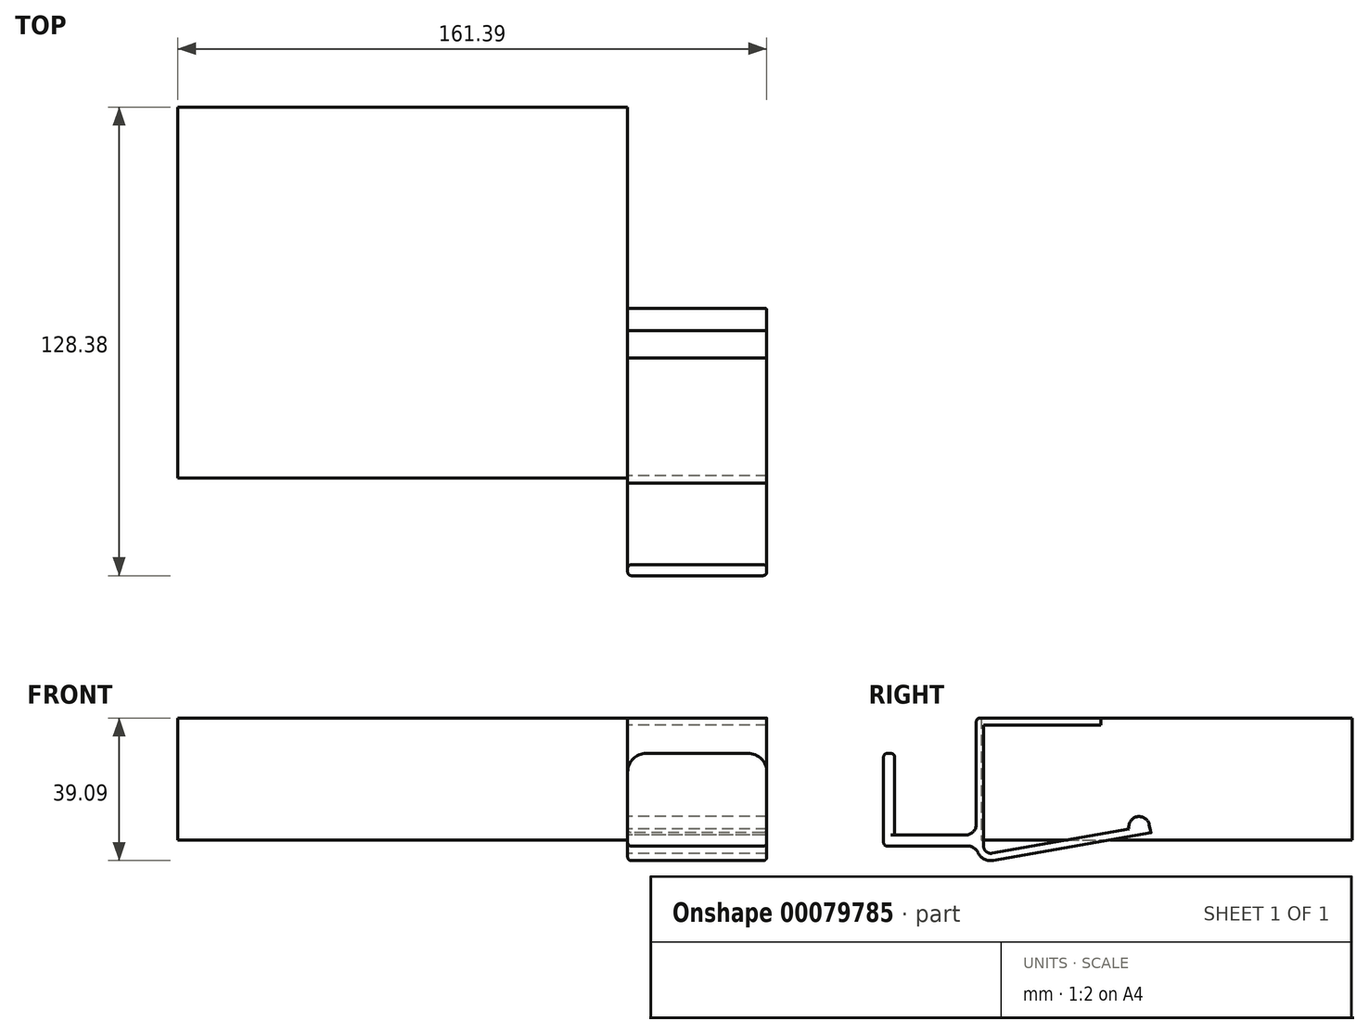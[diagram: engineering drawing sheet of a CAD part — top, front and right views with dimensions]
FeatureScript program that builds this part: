
annotation { "Feature Type Name" : "Feature", "Feature Type Description" : "" }
export const myFeature = defineFeature(function(context is Context, id is Id, definition is map)
    precondition{}
    {
        {
            var Q0;
            Q0=qCreatedBy(makeId("Right.planeOp"),FACE);
            var sketch = newSketch(context, id + "F0", { "sketchPlane" : qUnion([Q0])});
            skLineSegment(sketch, "E0.bottom", {"start": v(-53.16, 8.17) * mm, "end": v(48.44, 8.17) * mm});
            skLineSegment(sketch, "E0.top", {"start": v(-53.16, -25.23) * mm, "end": v(48.44, -25.23) * mm});
            skLineSegment(sketch, "E0.left", {"start": v(-53.16, 8.17) * mm, "end": v(-53.16, -25.23) * mm});
            skLineSegment(sketch, "E0.right", {"start": v(48.44, 8.17) * mm, "end": v(48.44, -25.23) * mm});
            skSolve(sketch);
        }
        {
            var Q0;
            Q0=makeQuery(id+"F0.imprint","IMPRINT",FACE,{"disambiguationData":[TD([[makeQuery(id+"F0.imprint","IMPRINT",EDGE,{"derivedFrom":sQuery(id+"F0.wireOp",EDGE,"E0.bottom")}),-1.0]])]});
            extrude(context, id + "F1", {"entities" : qUnion([Q0]), "depth" : 123.3 * mm});
        }
        {
            var Q0;
            Q0=makeQuery(id+"F1.opExtrude","CAP_FACE",FACE,{"disambiguationData":[OSD([sQuery(id+"F0.wireOp",EDGE,"E0.bottom"),sQuery(id+"F0.wireOp",EDGE,"E0.top"),sQuery(id+"F0.wireOp",EDGE,"E0.left"),sQuery(id+"F0.wireOp",EDGE,"E0.right")])],"isStart":false});
            var sketch = newSketch(context, id + "F2", { "sketchPlane" : qUnion([Q0])});
            skLineSegment(sketch, "E1", {"start": v(-20.37, 8.17) * mm, "end": v(-53.54, 8.17) * mm});
            skLineSegment(sketch, "E2", {"start": v(-54.54, 7.17) * mm, "end": v(-54.54, -23.92) * mm});
            skLineSegment(sketch, "E3", {"start": v(-49.85, -30.86) * mm, "end": v(-6.7, -23.25) * mm});
            skLineSegment(sketch, "E4.0", {"start": v(-20.37, 6.17) * mm, "end": v(-52.54, 6.17) * mm});
            skLineSegment(sketch, "E5.0", {"start": v(-52.54, 6.17) * mm, "end": v(-52.54, -26.92) * mm});
            skArc(sketch, "E6", {"start": v(-7.2, -21.03) * mm, "mid": v(-10.57, -18.9) * mm, "end": v(-12.7, -22.28) * mm});
            skLineSegment(sketch, "E7", {"start": v(-7.2, -21.03) * mm, "end": v(-6.7, -23.25) * mm});
            skLineSegment(sketch, "E8", {"start": v(-20.37, 8.17) * mm, "end": v(-20.37, 6.17) * mm});
            skLineSegment(sketch, "E9.trimOffspring", {"start": v(-50.2, -28.9) * mm, "end": v(-12.7, -22.28) * mm});
            skPoint(sketch, "E10.visualSharp", {"position": v(-54.54, -31.7) * mm});
            skArc(sketch, "E10.filletArc", {"start": v(-54.54, -26.92) * mm, "mid": v(-53.11, -29.99) * mm, "end": v(-49.85, -30.86) * mm});
            skPoint(sketch, "E11.visualSharp", {"position": v(-52.54, -29.3) * mm});
            skArc(sketch, "E11.filletArc", {"start": v(-52.54, -26.92) * mm, "mid": v(-51.83, -28.46) * mm, "end": v(-50.2, -28.9) * mm});
            skPoint(sketch, "E12.visualSharp", {"position": v(-54.54, 8.17) * mm});
            skArc(sketch, "E12.filletArc", {"start": v(-53.54, 8.17) * mm, "mid": v(-54.25, 7.88) * mm, "end": v(-54.54, 7.17) * mm});
            skLineSegment(sketch, "E13", {"start": v(-54.54, -26.92) * mm, "end": v(-79.94, -26.92) * mm});
            skLineSegment(sketch, "E14", {"start": v(-79.94, -26.92) * mm, "end": v(-79.94, -23.92) * mm});
            skLineSegment(sketch, "E15", {"start": v(-76.94, -23.92) * mm, "end": v(-54.54, -23.92) * mm});
            skLineSegment(sketch, "E16", {"start": v(-79.94, -23.92) * mm, "end": v(-79.94, -1.52) * mm});
            skLineSegment(sketch, "E17", {"start": v(-76.94, -1.52) * mm, "end": v(-76.94, -23.92) * mm});
            skLineSegment(sketch, "E18", {"start": v(-79.94, -1.52) * mm, "end": v(-76.94, -1.52) * mm});
            skSolve(sketch);
        }
        {
            var Q0;
            Q0 = qSketchRegion(id + "F2", true);
            extrude(context, id + "F3", {"entities" : qUnion([Q0]), "depth" : 38.1 * mm});
        }
        {
            var Q0;
            Q0=makeQuery(id+"F3.opExtrude","SWEPT_EDGE",EDGE,{"disambiguationData":[OSD([sQuery(id+"F2.wireOp",EDGE,"E13"),sQuery(id+"F2.wireOp",EDGE,"E14")])]});
            fillet(context, id + "F4", {"entities" : qUnion([Q0]), "radius" : 1 * mm, "tangentPropagation" : true, "allowEdgeOverflow" : false});
        }
        {
            var Q0;
            Q0=makeQuery(id+"F3.opExtrude","SWEPT_EDGE",EDGE,{"disambiguationData":[OSD([sQuery(id+"F2.wireOp",EDGE,"E2"),sQuery(id+"F2.wireOp",EDGE,"E15")])]});
            var Q1;
            Q1=makeQuery(id+"F3.opExtrude","SWEPT_EDGE",EDGE,{"disambiguationData":[OSD([sQuery(id+"F2.wireOp",EDGE,"E10.filletArc"),sQuery(id+"F2.wireOp",EDGE,"E13")])]});
            fillet(context, id + "F5", {"entities" : qUnion([Q0, Q1]), "radius" : 3 * mm, "tangentPropagation" : true, "allowEdgeOverflow" : false});
        }
        {
            var Q0;
            Q0=makeQuery(id+"F3.opExtrude","CAP_EDGE",EDGE,{"disambiguationData":[OSD([sQuery(id+"F2.wireOp",EDGE,"E18")])],"isStart":true});
            var Q1;
            Q1=makeQuery(id+"F3.opExtrude","CAP_EDGE",EDGE,{"disambiguationData":[OSD([sQuery(id+"F2.wireOp",EDGE,"E18")])],"isStart":false});
            fillet(context, id + "F6", {"entities" : qUnion([Q0, Q1]), "radius" : 5.08 * mm, "tangentPropagation" : true, "allowEdgeOverflow" : false});
        }
        {
            var Q0;
            {var subQ0=sQuery(id+"F2.wireOp",EDGE,"E18");Q0=makeQuery(id+"F6.opFillet","BLEND_FACE",FACE,{"disambiguationData":[OSD([subQ0]),TDD([makeQuery(id+"F3.opExtrude","CAP_EDGE",EDGE,{"disambiguationData":[OSD([subQ0])],"isStart":false})])]});}
            var Q1;
            Q1=makeQuery(id+"F3.opExtrude","SWEPT_FACE",FACE,{"disambiguationData":[OSD([sQuery(id+"F2.wireOp",EDGE,"E18")])]});
            var Q2;
            {var subQ0=sQuery(id+"F2.wireOp",EDGE,"E18");Q2=makeQuery(id+"F6.opFillet","BLEND_FACE",FACE,{"disambiguationData":[OSD([subQ0]),TDD([makeQuery(id+"F3.opExtrude","CAP_EDGE",EDGE,{"disambiguationData":[OSD([subQ0])],"isStart":true})])]});}
            fillet(context, id + "F7", {"entities" : qUnion([Q0, Q1, Q2]), "radius" : 1 * mm, "tangentPropagation" : true, "allowEdgeOverflow" : false});
        }
    });
